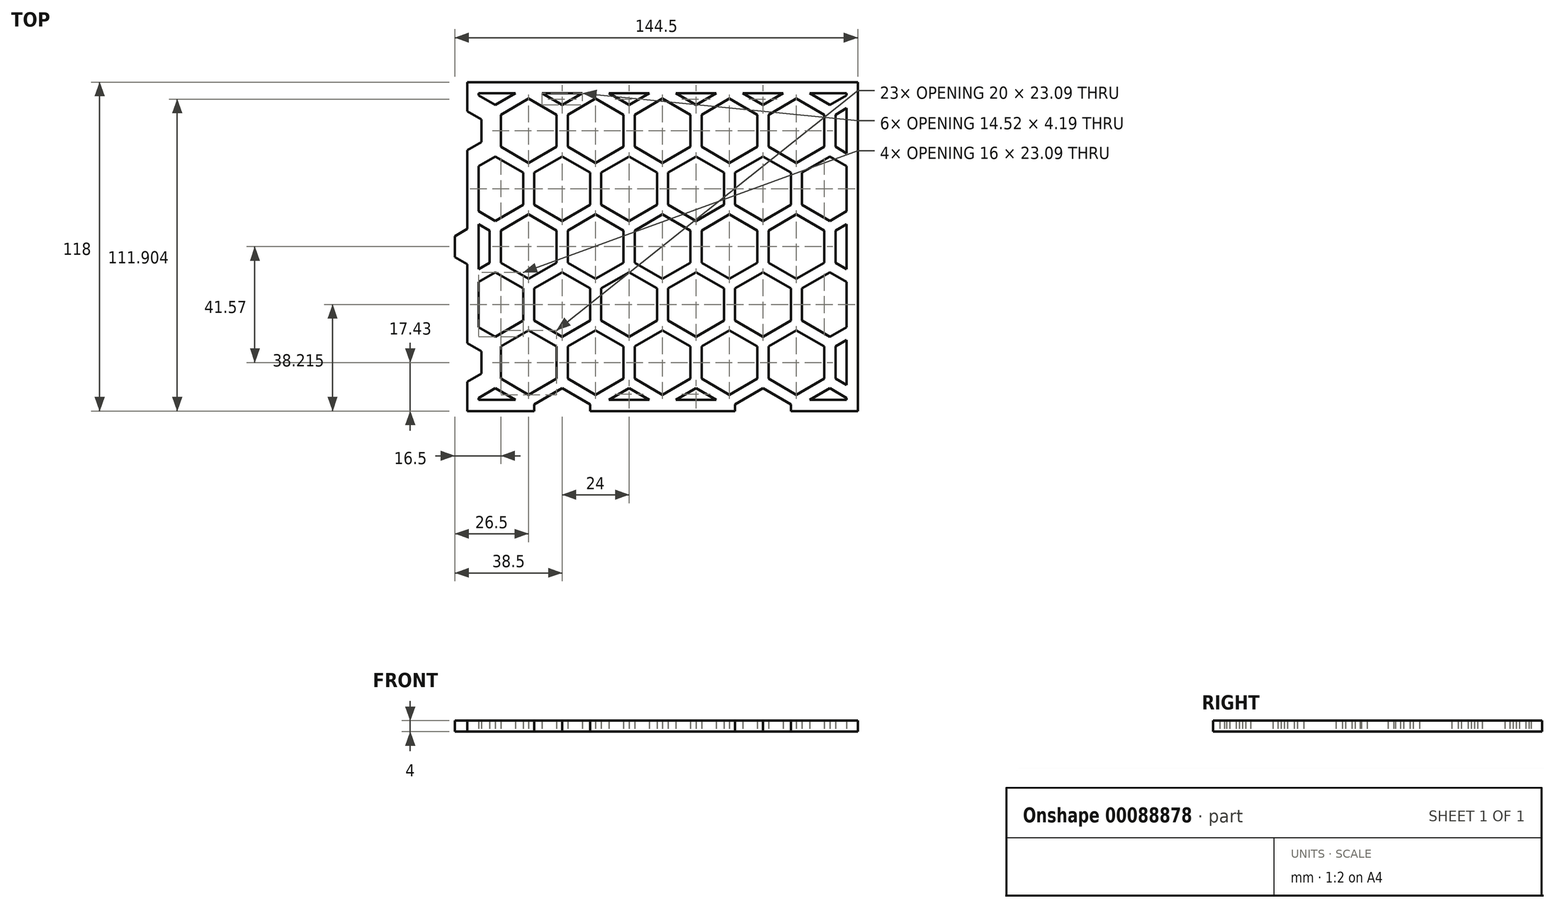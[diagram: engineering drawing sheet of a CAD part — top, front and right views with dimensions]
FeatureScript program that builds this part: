
annotation { "Feature Type Name" : "Feature", "Feature Type Description" : "" }
export const myFeature = defineFeature(function(context is Context, id is Id, definition is map)
    precondition{}
    {
        {
            var Q0;
            Q0=qCreatedBy(makeId("Top.planeOp"),FACE);
            var sketch = newSketch(context, id + "F0", { "sketchPlane" : qUnion([Q0])});
            skLineSegment(sketch, "E0.bottom", {"start": v(70, -59) * mm, "end": v(-70, -59) * mm});
            skLineSegment(sketch, "E0.top", {"start": v(70, 59) * mm, "end": v(-70, 59) * mm});
            skLineSegment(sketch, "E0.left", {"start": v(70, -59) * mm, "end": v(70, 59) * mm});
            skLineSegment(sketch, "E0.right", {"start": v(-70, -59) * mm, "end": v(-70, 59) * mm});
            skPoint(sketch, "E0.middle", {"position": v(0, 0) * mm});
            skLineSegment(sketch, "E1.0", {"start": v(-66, -55) * mm, "end": v(-66, 55) * mm});
            skLineSegment(sketch, "E1.1", {"start": v(66, -55) * mm, "end": v(-66, -55) * mm});
            skLineSegment(sketch, "E1.2", {"start": v(66, -55) * mm, "end": v(66, 55) * mm});
            skLineSegment(sketch, "E1.3", {"start": v(66, 55) * mm, "end": v(-66, 55) * mm});
            skSolve(sketch);
        }
        {
            var Q0;
            Q0 = qSketchRegion(id + "F0", true);
            extrude(context, id + "F1", {"entities" : qUnion([Q0]), "depth" : 4 * mm});
        }
        {
            var Q0;
            Q0=qCreatedBy(makeId("Top.planeOp"),FACE);
            var sketch = newSketch(context, id + "F2", { "sketchPlane" : qUnion([Q0])});
            skLineSegment(sketch, "E2.0.1.1", {"start": v(-62, -47.34) * mm, "end": v(-66, -49.65) * mm});
            skLineSegment(sketch, "E2.0.1.5", {"start": v(-66, -33.49) * mm, "end": v(-62, -35.8) * mm});
            skLineSegment(sketch, "E2.0.1.13", {"start": v(-62, -35.8) * mm, "end": v(-62, -47.34) * mm});
            skLineSegment(sketch, "E2.0.2.1", {"start": v(-62, -5.77) * mm, "end": v(-66, -8.08) * mm});
            skLineSegment(sketch, "E2.0.2.5", {"start": v(-66, 8.08) * mm, "end": v(-62, 5.77) * mm});
            skLineSegment(sketch, "E2.0.2.13", {"start": v(-62, 5.77) * mm, "end": v(-62, -5.77) * mm});
            skLineSegment(sketch, "E2.0.3.1", {"start": v(-62, 35.8) * mm, "end": v(-66, 33.49) * mm});
            skLineSegment(sketch, "E2.0.3.5", {"start": v(-66, 49.65) * mm, "end": v(-62, 47.34) * mm});
            skLineSegment(sketch, "E2.0.3.13", {"start": v(-62, 47.34) * mm, "end": v(-62, 35.8) * mm});
            skLineSegment(sketch, "E2.1.0.7", {"start": v(-60, -50.8) * mm, "end": v(-52.74, -55) * mm});
            skLineSegment(sketch, "E2.1.0.8", {"start": v(-66, -54.27) * mm, "end": v(-60, -50.8) * mm});
            skCircle(sketch, "E2.1.1.0", {"center": v(-48, -41.57) * mm, "radius": 11.55 * mm, "construction": true});
            skLineSegment(sketch, "E2.1.1.1", {"start": v(-38, -47.34) * mm, "end": v(-48, -53.12) * mm});
            skLineSegment(sketch, "E2.1.1.2", {"start": v(-48, -53.12) * mm, "end": v(-58, -47.34) * mm});
            skLineSegment(sketch, "E2.1.1.3", {"start": v(-58, -47.34) * mm, "end": v(-58, -35.8) * mm});
            skLineSegment(sketch, "E2.1.1.4", {"start": v(-58, -35.8) * mm, "end": v(-48, -30.02) * mm});
            skLineSegment(sketch, "E2.1.1.5", {"start": v(-48, -30.02) * mm, "end": v(-38, -35.8) * mm});
            skLineSegment(sketch, "E2.1.1.6", {"start": v(-50, -15.01) * mm, "end": v(-50, -26.56) * mm});
            skLineSegment(sketch, "E2.1.1.7", {"start": v(-60, -9.24) * mm, "end": v(-50, -15.01) * mm});
            skLineSegment(sketch, "E2.1.1.8", {"start": v(-66, -12.7) * mm, "end": v(-60, -9.24) * mm});
            skLineSegment(sketch, "E2.1.1.10", {"start": v(-60, -32.33) * mm, "end": v(-66, -28.87) * mm});
            skLineSegment(sketch, "E2.1.1.11", {"start": v(-50, -26.56) * mm, "end": v(-60, -32.33) * mm});
            skLineSegment(sketch, "E2.1.1.13", {"start": v(-38, -35.8) * mm, "end": v(-38, -47.34) * mm});
            skCircle(sketch, "E2.1.2.0", {"center": v(-48, 0) * mm, "radius": 11.55 * mm, "construction": true});
            skLineSegment(sketch, "E2.1.2.1", {"start": v(-38, -5.77) * mm, "end": v(-48, -11.55) * mm});
            skLineSegment(sketch, "E2.1.2.2", {"start": v(-48, -11.55) * mm, "end": v(-58, -5.77) * mm});
            skLineSegment(sketch, "E2.1.2.3", {"start": v(-58, -5.77) * mm, "end": v(-58, 5.77) * mm});
            skLineSegment(sketch, "E2.1.2.4", {"start": v(-58, 5.77) * mm, "end": v(-48, 11.55) * mm});
            skLineSegment(sketch, "E2.1.2.5", {"start": v(-48, 11.55) * mm, "end": v(-38, 5.77) * mm});
            skLineSegment(sketch, "E2.1.2.6", {"start": v(-50, 26.56) * mm, "end": v(-50, 15.01) * mm});
            skLineSegment(sketch, "E2.1.2.7", {"start": v(-60, 32.33) * mm, "end": v(-50, 26.56) * mm});
            skLineSegment(sketch, "E2.1.2.8", {"start": v(-66, 28.87) * mm, "end": v(-60, 32.33) * mm});
            skLineSegment(sketch, "E2.1.2.10", {"start": v(-60, 9.24) * mm, "end": v(-66, 12.7) * mm});
            skLineSegment(sketch, "E2.1.2.11", {"start": v(-50, 15.01) * mm, "end": v(-60, 9.24) * mm});
            skLineSegment(sketch, "E2.1.2.13", {"start": v(-38, 5.77) * mm, "end": v(-38, -5.77) * mm});
            skCircle(sketch, "E2.1.3.0", {"center": v(-48, 41.57) * mm, "radius": 11.55 * mm, "construction": true});
            skLineSegment(sketch, "E2.1.3.1", {"start": v(-38, 35.8) * mm, "end": v(-48, 30.02) * mm});
            skLineSegment(sketch, "E2.1.3.2", {"start": v(-48, 30.02) * mm, "end": v(-58, 35.8) * mm});
            skLineSegment(sketch, "E2.1.3.3", {"start": v(-58, 35.8) * mm, "end": v(-58, 47.34) * mm});
            skLineSegment(sketch, "E2.1.3.4", {"start": v(-58, 47.34) * mm, "end": v(-48, 53.12) * mm});
            skLineSegment(sketch, "E2.1.3.5", {"start": v(-48, 53.12) * mm, "end": v(-38, 47.34) * mm});
            skLineSegment(sketch, "E2.1.3.10", {"start": v(-60, 50.8) * mm, "end": v(-66, 54.27) * mm});
            skLineSegment(sketch, "E2.1.3.11", {"start": v(-52.74, 55) * mm, "end": v(-60, 50.8) * mm});
            skLineSegment(sketch, "E2.1.3.13", {"start": v(-38, 47.34) * mm, "end": v(-38, 35.8) * mm});
            skLineSegment(sketch, "E2.2.0.7", {"start": v(-36, -50.8) * mm, "end": v(-28.74, -55) * mm});
            skLineSegment(sketch, "E2.2.0.8", {"start": v(-43.26, -55) * mm, "end": v(-36, -50.8) * mm});
            skCircle(sketch, "E2.2.1.0", {"center": v(-24, -41.57) * mm, "radius": 11.55 * mm, "construction": true});
            skLineSegment(sketch, "E2.2.1.1", {"start": v(-14, -47.34) * mm, "end": v(-24, -53.12) * mm});
            skLineSegment(sketch, "E2.2.1.2", {"start": v(-24, -53.12) * mm, "end": v(-34, -47.34) * mm});
            skLineSegment(sketch, "E2.2.1.3", {"start": v(-34, -47.34) * mm, "end": v(-34, -35.8) * mm});
            skLineSegment(sketch, "E2.2.1.4", {"start": v(-34, -35.8) * mm, "end": v(-24, -30.02) * mm});
            skLineSegment(sketch, "E2.2.1.5", {"start": v(-24, -30.02) * mm, "end": v(-14, -35.8) * mm});
            skLineSegment(sketch, "E2.2.1.6", {"start": v(-26, -15.01) * mm, "end": v(-26, -26.56) * mm});
            skLineSegment(sketch, "E2.2.1.7", {"start": v(-36, -9.24) * mm, "end": v(-26, -15.01) * mm});
            skLineSegment(sketch, "E2.2.1.8", {"start": v(-46, -15.01) * mm, "end": v(-36, -9.24) * mm});
            skLineSegment(sketch, "E2.2.1.9", {"start": v(-46, -26.56) * mm, "end": v(-46, -15.01) * mm});
            skLineSegment(sketch, "E2.2.1.10", {"start": v(-36, -32.33) * mm, "end": v(-46, -26.56) * mm});
            skLineSegment(sketch, "E2.2.1.11", {"start": v(-26, -26.56) * mm, "end": v(-36, -32.33) * mm});
            skCircle(sketch, "E2.2.1.12", {"center": v(-36, -20.79) * mm, "radius": 11.55 * mm, "construction": true});
            skLineSegment(sketch, "E2.2.1.13", {"start": v(-14, -35.8) * mm, "end": v(-14, -47.34) * mm});
            skCircle(sketch, "E2.2.2.0", {"center": v(-24, 0) * mm, "radius": 11.55 * mm, "construction": true});
            skLineSegment(sketch, "E2.2.2.1", {"start": v(-14, -5.77) * mm, "end": v(-24, -11.55) * mm});
            skLineSegment(sketch, "E2.2.2.2", {"start": v(-24, -11.55) * mm, "end": v(-34, -5.77) * mm});
            skLineSegment(sketch, "E2.2.2.3", {"start": v(-34, -5.77) * mm, "end": v(-34, 5.77) * mm});
            skLineSegment(sketch, "E2.2.2.4", {"start": v(-34, 5.77) * mm, "end": v(-24, 11.55) * mm});
            skLineSegment(sketch, "E2.2.2.5", {"start": v(-24, 11.55) * mm, "end": v(-14, 5.77) * mm});
            skLineSegment(sketch, "E2.2.2.6", {"start": v(-26, 26.56) * mm, "end": v(-26, 15.01) * mm});
            skLineSegment(sketch, "E2.2.2.7", {"start": v(-36, 32.33) * mm, "end": v(-26, 26.56) * mm});
            skLineSegment(sketch, "E2.2.2.8", {"start": v(-46, 26.56) * mm, "end": v(-36, 32.33) * mm});
            skLineSegment(sketch, "E2.2.2.9", {"start": v(-46, 15.01) * mm, "end": v(-46, 26.56) * mm});
            skLineSegment(sketch, "E2.2.2.10", {"start": v(-36, 9.24) * mm, "end": v(-46, 15.01) * mm});
            skLineSegment(sketch, "E2.2.2.11", {"start": v(-26, 15.01) * mm, "end": v(-36, 9.24) * mm});
            skCircle(sketch, "E2.2.2.12", {"center": v(-36, 20.78) * mm, "radius": 11.55 * mm, "construction": true});
            skLineSegment(sketch, "E2.2.2.13", {"start": v(-14, 5.77) * mm, "end": v(-14, -5.77) * mm});
            skCircle(sketch, "E2.2.3.0", {"center": v(-24, 41.57) * mm, "radius": 11.55 * mm, "construction": true});
            skLineSegment(sketch, "E2.2.3.1", {"start": v(-14, 35.8) * mm, "end": v(-24, 30.02) * mm});
            skLineSegment(sketch, "E2.2.3.2", {"start": v(-24, 30.02) * mm, "end": v(-34, 35.8) * mm});
            skLineSegment(sketch, "E2.2.3.3", {"start": v(-34, 35.8) * mm, "end": v(-34, 47.34) * mm});
            skLineSegment(sketch, "E2.2.3.4", {"start": v(-34, 47.34) * mm, "end": v(-24, 53.12) * mm});
            skLineSegment(sketch, "E2.2.3.5", {"start": v(-24, 53.12) * mm, "end": v(-14, 47.34) * mm});
            skLineSegment(sketch, "E2.2.3.10", {"start": v(-36, 50.8) * mm, "end": v(-43.26, 55) * mm});
            skLineSegment(sketch, "E2.2.3.11", {"start": v(-28.74, 55) * mm, "end": v(-36, 50.8) * mm});
            skLineSegment(sketch, "E2.2.3.13", {"start": v(-14, 47.34) * mm, "end": v(-14, 35.8) * mm});
            skLineSegment(sketch, "E2.3.0.7", {"start": v(-12, -50.8) * mm, "end": v(-4.74, -55) * mm});
            skLineSegment(sketch, "E2.3.0.8", {"start": v(-19.26, -55) * mm, "end": v(-12, -50.8) * mm});
            skCircle(sketch, "E2.3.1.0", {"center": v(0, -41.57) * mm, "radius": 11.55 * mm, "construction": true});
            skLineSegment(sketch, "E2.3.1.1", {"start": v(10, -47.34) * mm, "end": v(0, -53.12) * mm});
            skLineSegment(sketch, "E2.3.1.2", {"start": v(0, -53.12) * mm, "end": v(-10, -47.34) * mm});
            skLineSegment(sketch, "E2.3.1.3", {"start": v(-10, -47.34) * mm, "end": v(-10, -35.8) * mm});
            skLineSegment(sketch, "E2.3.1.4", {"start": v(-10, -35.8) * mm, "end": v(0, -30.02) * mm});
            skLineSegment(sketch, "E2.3.1.5", {"start": v(0, -30.02) * mm, "end": v(10, -35.8) * mm});
            skLineSegment(sketch, "E2.3.1.6", {"start": v(-2, -15.01) * mm, "end": v(-2, -26.56) * mm});
            skLineSegment(sketch, "E2.3.1.7", {"start": v(-12, -9.24) * mm, "end": v(-2, -15.01) * mm});
            skLineSegment(sketch, "E2.3.1.8", {"start": v(-22, -15.01) * mm, "end": v(-12, -9.24) * mm});
            skLineSegment(sketch, "E2.3.1.9", {"start": v(-22, -26.56) * mm, "end": v(-22, -15.01) * mm});
            skLineSegment(sketch, "E2.3.1.10", {"start": v(-12, -32.33) * mm, "end": v(-22, -26.56) * mm});
            skLineSegment(sketch, "E2.3.1.11", {"start": v(-2, -26.56) * mm, "end": v(-12, -32.33) * mm});
            skCircle(sketch, "E2.3.1.12", {"center": v(-12, -20.79) * mm, "radius": 11.55 * mm, "construction": true});
            skLineSegment(sketch, "E2.3.1.13", {"start": v(10, -35.8) * mm, "end": v(10, -47.34) * mm});
            skCircle(sketch, "E2.3.2.0", {"center": v(0, 0) * mm, "radius": 11.55 * mm, "construction": true});
            skLineSegment(sketch, "E2.3.2.1", {"start": v(10, -5.77) * mm, "end": v(0, -11.55) * mm});
            skLineSegment(sketch, "E2.3.2.2", {"start": v(0, -11.55) * mm, "end": v(-10, -5.77) * mm});
            skLineSegment(sketch, "E2.3.2.3", {"start": v(-10, -5.77) * mm, "end": v(-10, 5.77) * mm});
            skLineSegment(sketch, "E2.3.2.4", {"start": v(-10, 5.77) * mm, "end": v(0, 11.55) * mm});
            skLineSegment(sketch, "E2.3.2.5", {"start": v(0, 11.55) * mm, "end": v(10, 5.77) * mm});
            skLineSegment(sketch, "E2.3.2.6", {"start": v(-2, 26.56) * mm, "end": v(-2, 15.01) * mm});
            skLineSegment(sketch, "E2.3.2.7", {"start": v(-12, 32.33) * mm, "end": v(-2, 26.56) * mm});
            skLineSegment(sketch, "E2.3.2.8", {"start": v(-22, 26.56) * mm, "end": v(-12, 32.33) * mm});
            skLineSegment(sketch, "E2.3.2.9", {"start": v(-22, 15.01) * mm, "end": v(-22, 26.56) * mm});
            skLineSegment(sketch, "E2.3.2.10", {"start": v(-12, 9.24) * mm, "end": v(-22, 15.01) * mm});
            skLineSegment(sketch, "E2.3.2.11", {"start": v(-2, 15.01) * mm, "end": v(-12, 9.24) * mm});
            skCircle(sketch, "E2.3.2.12", {"center": v(-12, 20.78) * mm, "radius": 11.55 * mm, "construction": true});
            skLineSegment(sketch, "E2.3.2.13", {"start": v(10, 5.77) * mm, "end": v(10, -5.77) * mm});
            skCircle(sketch, "E2.3.3.0", {"center": v(0, 41.57) * mm, "radius": 11.55 * mm, "construction": true});
            skLineSegment(sketch, "E2.3.3.1", {"start": v(10, 35.8) * mm, "end": v(0, 30.02) * mm});
            skLineSegment(sketch, "E2.3.3.2", {"start": v(0, 30.02) * mm, "end": v(-10, 35.8) * mm});
            skLineSegment(sketch, "E2.3.3.3", {"start": v(-10, 35.8) * mm, "end": v(-10, 47.34) * mm});
            skLineSegment(sketch, "E2.3.3.4", {"start": v(-10, 47.34) * mm, "end": v(0, 53.12) * mm});
            skLineSegment(sketch, "E2.3.3.5", {"start": v(0, 53.12) * mm, "end": v(10, 47.34) * mm});
            skLineSegment(sketch, "E2.3.3.10", {"start": v(-12, 50.8) * mm, "end": v(-19.26, 55) * mm});
            skLineSegment(sketch, "E2.3.3.11", {"start": v(-4.74, 55) * mm, "end": v(-12, 50.8) * mm});
            skLineSegment(sketch, "E2.3.3.13", {"start": v(10, 47.34) * mm, "end": v(10, 35.8) * mm});
            skLineSegment(sketch, "E2.4.0.7", {"start": v(12, -50.8) * mm, "end": v(19.26, -55) * mm});
            skLineSegment(sketch, "E2.4.0.8", {"start": v(4.74, -55) * mm, "end": v(12, -50.8) * mm});
            skCircle(sketch, "E2.4.1.0", {"center": v(24, -41.57) * mm, "radius": 11.55 * mm, "construction": true});
            skLineSegment(sketch, "E2.4.1.1", {"start": v(34, -47.34) * mm, "end": v(24, -53.12) * mm});
            skLineSegment(sketch, "E2.4.1.2", {"start": v(24, -53.12) * mm, "end": v(14, -47.34) * mm});
            skLineSegment(sketch, "E2.4.1.3", {"start": v(14, -47.34) * mm, "end": v(14, -35.8) * mm});
            skLineSegment(sketch, "E2.4.1.4", {"start": v(14, -35.8) * mm, "end": v(24, -30.02) * mm});
            skLineSegment(sketch, "E2.4.1.5", {"start": v(24, -30.02) * mm, "end": v(34, -35.8) * mm});
            skLineSegment(sketch, "E2.4.1.6", {"start": v(22, -15.01) * mm, "end": v(22, -26.56) * mm});
            skLineSegment(sketch, "E2.4.1.7", {"start": v(12, -9.24) * mm, "end": v(22, -15.01) * mm});
            skLineSegment(sketch, "E2.4.1.8", {"start": v(2, -15.01) * mm, "end": v(12, -9.24) * mm});
            skLineSegment(sketch, "E2.4.1.9", {"start": v(2, -26.56) * mm, "end": v(2, -15.01) * mm});
            skLineSegment(sketch, "E2.4.1.10", {"start": v(12, -32.33) * mm, "end": v(2, -26.56) * mm});
            skLineSegment(sketch, "E2.4.1.11", {"start": v(22, -26.56) * mm, "end": v(12, -32.33) * mm});
            skCircle(sketch, "E2.4.1.12", {"center": v(12, -20.79) * mm, "radius": 11.55 * mm, "construction": true});
            skLineSegment(sketch, "E2.4.1.13", {"start": v(34, -35.8) * mm, "end": v(34, -47.34) * mm});
            skCircle(sketch, "E2.4.2.0", {"center": v(24, 0) * mm, "radius": 11.55 * mm, "construction": true});
            skLineSegment(sketch, "E2.4.2.1", {"start": v(34, -5.77) * mm, "end": v(24, -11.55) * mm});
            skLineSegment(sketch, "E2.4.2.2", {"start": v(24, -11.55) * mm, "end": v(14, -5.77) * mm});
            skLineSegment(sketch, "E2.4.2.3", {"start": v(14, -5.77) * mm, "end": v(14, 5.77) * mm});
            skLineSegment(sketch, "E2.4.2.4", {"start": v(14, 5.77) * mm, "end": v(24, 11.55) * mm});
            skLineSegment(sketch, "E2.4.2.5", {"start": v(24, 11.55) * mm, "end": v(34, 5.77) * mm});
            skLineSegment(sketch, "E2.4.2.6", {"start": v(22, 26.56) * mm, "end": v(22, 15.01) * mm});
            skLineSegment(sketch, "E2.4.2.7", {"start": v(12, 32.33) * mm, "end": v(22, 26.56) * mm});
            skLineSegment(sketch, "E2.4.2.8", {"start": v(2, 26.56) * mm, "end": v(12, 32.33) * mm});
            skLineSegment(sketch, "E2.4.2.9", {"start": v(2, 15.01) * mm, "end": v(2, 26.56) * mm});
            skLineSegment(sketch, "E2.4.2.10", {"start": v(12, 9.24) * mm, "end": v(2, 15.01) * mm});
            skLineSegment(sketch, "E2.4.2.11", {"start": v(22, 15.01) * mm, "end": v(12, 9.24) * mm});
            skCircle(sketch, "E2.4.2.12", {"center": v(12, 20.78) * mm, "radius": 11.55 * mm, "construction": true});
            skLineSegment(sketch, "E2.4.2.13", {"start": v(34, 5.77) * mm, "end": v(34, -5.77) * mm});
            skCircle(sketch, "E2.4.3.0", {"center": v(24, 41.57) * mm, "radius": 11.55 * mm, "construction": true});
            skLineSegment(sketch, "E2.4.3.1", {"start": v(34, 35.8) * mm, "end": v(24, 30.02) * mm});
            skLineSegment(sketch, "E2.4.3.2", {"start": v(24, 30.02) * mm, "end": v(14, 35.8) * mm});
            skLineSegment(sketch, "E2.4.3.3", {"start": v(14, 35.8) * mm, "end": v(14, 47.34) * mm});
            skLineSegment(sketch, "E2.4.3.4", {"start": v(14, 47.34) * mm, "end": v(24, 53.12) * mm});
            skLineSegment(sketch, "E2.4.3.5", {"start": v(24, 53.12) * mm, "end": v(34, 47.34) * mm});
            skLineSegment(sketch, "E2.4.3.10", {"start": v(12, 50.8) * mm, "end": v(4.74, 55) * mm});
            skLineSegment(sketch, "E2.4.3.11", {"start": v(19.26, 55) * mm, "end": v(12, 50.8) * mm});
            skLineSegment(sketch, "E2.4.3.13", {"start": v(34, 47.34) * mm, "end": v(34, 35.8) * mm});
            skLineSegment(sketch, "E2.5.0.7", {"start": v(36, -50.8) * mm, "end": v(43.26, -55) * mm});
            skLineSegment(sketch, "E2.5.0.8", {"start": v(28.74, -55) * mm, "end": v(36, -50.8) * mm});
            skCircle(sketch, "E2.5.1.0", {"center": v(48, -41.57) * mm, "radius": 11.55 * mm, "construction": true});
            skLineSegment(sketch, "E2.5.1.1", {"start": v(58, -47.34) * mm, "end": v(48, -53.12) * mm});
            skLineSegment(sketch, "E2.5.1.2", {"start": v(48, -53.12) * mm, "end": v(38, -47.34) * mm});
            skLineSegment(sketch, "E2.5.1.3", {"start": v(38, -47.34) * mm, "end": v(38, -35.8) * mm});
            skLineSegment(sketch, "E2.5.1.4", {"start": v(38, -35.8) * mm, "end": v(48, -30.02) * mm});
            skLineSegment(sketch, "E2.5.1.5", {"start": v(48, -30.02) * mm, "end": v(58, -35.8) * mm});
            skLineSegment(sketch, "E2.5.1.6", {"start": v(46, -15.01) * mm, "end": v(46, -26.56) * mm});
            skLineSegment(sketch, "E2.5.1.7", {"start": v(36, -9.24) * mm, "end": v(46, -15.01) * mm});
            skLineSegment(sketch, "E2.5.1.8", {"start": v(26, -15.01) * mm, "end": v(36, -9.24) * mm});
            skLineSegment(sketch, "E2.5.1.9", {"start": v(26, -26.56) * mm, "end": v(26, -15.01) * mm});
            skLineSegment(sketch, "E2.5.1.10", {"start": v(36, -32.33) * mm, "end": v(26, -26.56) * mm});
            skLineSegment(sketch, "E2.5.1.11", {"start": v(46, -26.56) * mm, "end": v(36, -32.33) * mm});
            skCircle(sketch, "E2.5.1.12", {"center": v(36, -20.79) * mm, "radius": 11.55 * mm, "construction": true});
            skLineSegment(sketch, "E2.5.1.13", {"start": v(58, -35.8) * mm, "end": v(58, -47.34) * mm});
            skCircle(sketch, "E2.5.2.0", {"center": v(48, 0) * mm, "radius": 11.55 * mm, "construction": true});
            skLineSegment(sketch, "E2.5.2.1", {"start": v(58, -5.77) * mm, "end": v(48, -11.55) * mm});
            skLineSegment(sketch, "E2.5.2.2", {"start": v(48, -11.55) * mm, "end": v(38, -5.77) * mm});
            skLineSegment(sketch, "E2.5.2.3", {"start": v(38, -5.77) * mm, "end": v(38, 5.77) * mm});
            skLineSegment(sketch, "E2.5.2.4", {"start": v(38, 5.77) * mm, "end": v(48, 11.55) * mm});
            skLineSegment(sketch, "E2.5.2.5", {"start": v(48, 11.55) * mm, "end": v(58, 5.77) * mm});
            skLineSegment(sketch, "E2.5.2.6", {"start": v(46, 26.56) * mm, "end": v(46, 15.01) * mm});
            skLineSegment(sketch, "E2.5.2.7", {"start": v(36, 32.33) * mm, "end": v(46, 26.56) * mm});
            skLineSegment(sketch, "E2.5.2.8", {"start": v(26, 26.56) * mm, "end": v(36, 32.33) * mm});
            skLineSegment(sketch, "E2.5.2.9", {"start": v(26, 15.01) * mm, "end": v(26, 26.56) * mm});
            skLineSegment(sketch, "E2.5.2.10", {"start": v(36, 9.24) * mm, "end": v(26, 15.01) * mm});
            skLineSegment(sketch, "E2.5.2.11", {"start": v(46, 15.01) * mm, "end": v(36, 9.24) * mm});
            skCircle(sketch, "E2.5.2.12", {"center": v(36, 20.78) * mm, "radius": 11.55 * mm, "construction": true});
            skLineSegment(sketch, "E2.5.2.13", {"start": v(58, 5.77) * mm, "end": v(58, -5.77) * mm});
            skCircle(sketch, "E2.5.3.0", {"center": v(48, 41.57) * mm, "radius": 11.55 * mm, "construction": true});
            skLineSegment(sketch, "E2.5.3.1", {"start": v(58, 35.8) * mm, "end": v(48, 30.02) * mm});
            skLineSegment(sketch, "E2.5.3.2", {"start": v(48, 30.02) * mm, "end": v(38, 35.8) * mm});
            skLineSegment(sketch, "E2.5.3.3", {"start": v(38, 35.8) * mm, "end": v(38, 47.34) * mm});
            skLineSegment(sketch, "E2.5.3.4", {"start": v(38, 47.34) * mm, "end": v(48, 53.12) * mm});
            skLineSegment(sketch, "E2.5.3.5", {"start": v(48, 53.12) * mm, "end": v(58, 47.34) * mm});
            skLineSegment(sketch, "E2.5.3.10", {"start": v(36, 50.8) * mm, "end": v(28.74, 55) * mm});
            skLineSegment(sketch, "E2.5.3.11", {"start": v(43.26, 55) * mm, "end": v(36, 50.8) * mm});
            skLineSegment(sketch, "E2.5.3.13", {"start": v(58, 47.34) * mm, "end": v(58, 35.8) * mm});
            skLineSegment(sketch, "E2.6.0.7", {"start": v(60, -50.8) * mm, "end": v(66, -54.27) * mm});
            skLineSegment(sketch, "E2.6.0.8", {"start": v(52.74, -55) * mm, "end": v(60, -50.8) * mm});
            skLineSegment(sketch, "E2.6.1.2", {"start": v(66, -49.65) * mm, "end": v(62, -47.34) * mm});
            skLineSegment(sketch, "E2.6.1.3", {"start": v(62, -47.34) * mm, "end": v(62, -35.8) * mm});
            skLineSegment(sketch, "E2.6.1.4", {"start": v(62, -35.8) * mm, "end": v(66, -33.49) * mm});
            skLineSegment(sketch, "E2.6.1.7", {"start": v(60, -9.24) * mm, "end": v(66, -12.7) * mm});
            skLineSegment(sketch, "E2.6.1.8", {"start": v(50, -15.01) * mm, "end": v(60, -9.24) * mm});
            skLineSegment(sketch, "E2.6.1.9", {"start": v(50, -26.56) * mm, "end": v(50, -15.01) * mm});
            skLineSegment(sketch, "E2.6.1.10", {"start": v(60, -32.33) * mm, "end": v(50, -26.56) * mm});
            skLineSegment(sketch, "E2.6.1.11", {"start": v(66, -28.87) * mm, "end": v(60, -32.33) * mm});
            skLineSegment(sketch, "E2.6.2.2", {"start": v(66, -8.08) * mm, "end": v(62, -5.77) * mm});
            skLineSegment(sketch, "E2.6.2.3", {"start": v(62, -5.77) * mm, "end": v(62, 5.77) * mm});
            skLineSegment(sketch, "E2.6.2.4", {"start": v(62, 5.77) * mm, "end": v(66, 8.08) * mm});
            skLineSegment(sketch, "E2.6.2.7", {"start": v(60, 32.33) * mm, "end": v(66, 28.87) * mm});
            skLineSegment(sketch, "E2.6.2.8", {"start": v(50, 26.56) * mm, "end": v(60, 32.33) * mm});
            skLineSegment(sketch, "E2.6.2.9", {"start": v(50, 15.01) * mm, "end": v(50, 26.56) * mm});
            skLineSegment(sketch, "E2.6.2.10", {"start": v(60, 9.24) * mm, "end": v(50, 15.01) * mm});
            skLineSegment(sketch, "E2.6.2.11", {"start": v(66, 12.7) * mm, "end": v(60, 9.24) * mm});
            skLineSegment(sketch, "E2.6.3.2", {"start": v(66, 33.49) * mm, "end": v(62, 35.8) * mm});
            skLineSegment(sketch, "E2.6.3.3", {"start": v(62, 35.8) * mm, "end": v(62, 47.34) * mm});
            skLineSegment(sketch, "E2.6.3.4", {"start": v(62, 47.34) * mm, "end": v(66, 49.65) * mm});
            skLineSegment(sketch, "E2.6.3.10", {"start": v(60, 50.8) * mm, "end": v(52.74, 55) * mm});
            skLineSegment(sketch, "E2.6.3.11", {"start": v(66, 54.27) * mm, "end": v(60, 50.8) * mm});
            skLineSegment(sketch, "E3.0", {"start": v(-66, -55) * mm, "end": v(-66, -54.27) * mm});
            skLineSegment(sketch, "E3.1", {"start": v(66, 55) * mm, "end": v(52.74, 55) * mm});
            skLineSegment(sketch, "E3.2", {"start": v(66, -55) * mm, "end": v(66, -54.27) * mm});
            skLineSegment(sketch, "E3.3", {"start": v(66, -55) * mm, "end": v(52.74, -55) * mm});
            skLineSegment(sketch, "E4.trimOffspring", {"start": v(-66, 54.27) * mm, "end": v(-66, 55) * mm});
            skLineSegment(sketch, "E5.trimOffspring", {"start": v(-66, 33.49) * mm, "end": v(-66, 49.65) * mm});
            skLineSegment(sketch, "E6.trimOffspring", {"start": v(-66, 12.7) * mm, "end": v(-66, 28.87) * mm});
            skLineSegment(sketch, "E7.trimOffspring", {"start": v(-52.74, 55) * mm, "end": v(-66, 55) * mm});
            skLineSegment(sketch, "E8.trimOffspring", {"start": v(-28.74, 55) * mm, "end": v(-43.26, 55) * mm});
            skLineSegment(sketch, "E9.trimOffspring", {"start": v(-4.74, 55) * mm, "end": v(-19.26, 55) * mm});
            skLineSegment(sketch, "E10.trimOffspring", {"start": v(19.26, 55) * mm, "end": v(4.74, 55) * mm});
            skLineSegment(sketch, "E11.trimOffspring", {"start": v(43.26, 55) * mm, "end": v(28.74, 55) * mm});
            skLineSegment(sketch, "E12.trimOffspring", {"start": v(66, 54.27) * mm, "end": v(66, 55) * mm});
            skLineSegment(sketch, "E13.trimOffspring", {"start": v(66, 33.49) * mm, "end": v(66, 49.65) * mm});
            skLineSegment(sketch, "E14.trimOffspring", {"start": v(66, 12.7) * mm, "end": v(66, 28.87) * mm});
            skLineSegment(sketch, "E15.trimOffspring", {"start": v(66, -8.08) * mm, "end": v(66, 8.08) * mm});
            skLineSegment(sketch, "E16.trimOffspring", {"start": v(66, -28.87) * mm, "end": v(66, -12.7) * mm});
            skLineSegment(sketch, "E17.trimOffspring", {"start": v(66, -49.65) * mm, "end": v(66, -33.49) * mm});
            skLineSegment(sketch, "E18.trimOffspring", {"start": v(43.26, -55) * mm, "end": v(28.74, -55) * mm});
            skLineSegment(sketch, "E19.trimOffspring", {"start": v(19.26, -55) * mm, "end": v(4.74, -55) * mm});
            skLineSegment(sketch, "E20.trimOffspring", {"start": v(-4.74, -55) * mm, "end": v(-19.26, -55) * mm});
            skLineSegment(sketch, "E21.trimOffspring", {"start": v(-28.74, -55) * mm, "end": v(-43.26, -55) * mm});
            skLineSegment(sketch, "E22.trimOffspring", {"start": v(-52.74, -55) * mm, "end": v(-66, -55) * mm});
            skLineSegment(sketch, "E23.trimOffspring", {"start": v(-66, -49.65) * mm, "end": v(-66, -33.49) * mm});
            skLineSegment(sketch, "E24.trimOffspring", {"start": v(-66, -28.87) * mm, "end": v(-66, -12.7) * mm});
            skLineSegment(sketch, "E25.trimOffspring", {"start": v(-66, -8.08) * mm, "end": v(-66, 8.08) * mm});
            skLineSegment(sketch, "E26.0", {"start": v(-70, -59) * mm, "end": v(-70, 59) * mm});
            skLineSegment(sketch, "E26.1", {"start": v(70, 59) * mm, "end": v(-70, 59) * mm});
            skLineSegment(sketch, "E26.2", {"start": v(70, -59) * mm, "end": v(70, 59) * mm});
            skLineSegment(sketch, "E26.3", {"start": v(70, -59) * mm, "end": v(-70, -59) * mm});
            skSolve(sketch);
        }
        {
            var Q0;
            Q0 = qSketchRegion(id + "F2", true);
            var Q1;
            Q1=makeQuery(id+"F1.opExtrude","CAP_FACE",FACE,{"disambiguationData":[OSD([sQuery(id+"F0.wireOp",EDGE,"E0.bottom"),sQuery(id+"F0.wireOp",EDGE,"E0.top"),sQuery(id+"F0.wireOp",EDGE,"E0.left"),sQuery(id+"F0.wireOp",EDGE,"E0.right"),sQuery(id+"F0.wireOp",EDGE,"E1.0"),sQuery(id+"F0.wireOp",EDGE,"E1.1"),sQuery(id+"F0.wireOp",EDGE,"E1.2"),sQuery(id+"F0.wireOp",EDGE,"E1.3")])],"isStart":false});
            extrude(context, id + "F3", {"entities" : qUnion([Q0]), "operationType" : NewBodyOperationType.ADD, "endBound" : BoundingType.UP_TO_SURFACE, "endBoundEntityFace" : qUnion([Q1]), "depth" : 4 * mm});
        }
        {
            var Q0;
            Q0=qCreatedBy(makeId("Top.planeOp"),FACE);
            var sketch = newSketch(context, id + "F4", { "sketchPlane" : qUnion([Q0])});
            skCircle(sketch, "E27.cCircle", {"center": v(36, -62.36) * mm, "radius": 11.55 * mm, "construction": true});
            skLineSegment(sketch, "E27.0", {"start": v(36, -73.9) * mm, "end": v(26, -68.13) * mm});
            skLineSegment(sketch, "E27.1", {"start": v(26, -68.13) * mm, "end": v(26, -56.58) * mm});
            skLineSegment(sketch, "E27.2", {"start": v(26, -56.58) * mm, "end": v(36, -50.8) * mm});
            skLineSegment(sketch, "E27.3", {"start": v(36, -50.8) * mm, "end": v(46, -56.58) * mm});
            skLineSegment(sketch, "E27.4", {"start": v(46, -56.58) * mm, "end": v(46, -68.13) * mm});
            skLineSegment(sketch, "E27.5", {"start": v(46, -68.13) * mm, "end": v(36, -73.9) * mm});
            skCircle(sketch, "E28.cCircle", {"center": v(-36, -62.36) * mm, "radius": 11.55 * mm, "construction": true});
            skLineSegment(sketch, "E28.0", {"start": v(-26, -68.13) * mm, "end": v(-36, -73.9) * mm});
            skLineSegment(sketch, "E28.1", {"start": v(-36, -73.9) * mm, "end": v(-46, -68.13) * mm});
            skLineSegment(sketch, "E28.2", {"start": v(-46, -68.13) * mm, "end": v(-46, -56.58) * mm});
            skLineSegment(sketch, "E28.3", {"start": v(-46, -56.58) * mm, "end": v(-36, -50.8) * mm});
            skLineSegment(sketch, "E28.4", {"start": v(-36, -50.8) * mm, "end": v(-26, -56.58) * mm});
            skLineSegment(sketch, "E28.5", {"start": v(-26, -56.58) * mm, "end": v(-26, -68.13) * mm});
            skSolve(sketch);
        }
        {
            var Q0;
            Q0 = qSketchRegion(id + "F4", true);
            extrude(context, id + "F5", {"entities" : qUnion([Q0]), "operationType" : NewBodyOperationType.REMOVE, "endBound" : BoundingType.THROUGH_ALL, "depth" : 25 * mm});
        }
        {
            var Q0;
            Q0=qCreatedBy(makeId("Top.planeOp"),FACE);
            var sketch = newSketch(context, id + "F6", { "sketchPlane" : qUnion([Q0])});
            skCircle(sketch, "E29.cCircle", {"center": v(-68, 0) * mm, "radius": 11.55 * mm, "construction": true});
            skLineSegment(sketch, "E29.1", {"start": v(-70, -10.4) * mm, "end": v(-78, -5.77) * mm, "construction": true});
            skLineSegment(sketch, "E29.2", {"start": v(-78, -5.77) * mm, "end": v(-78, 5.77) * mm, "construction": true});
            skLineSegment(sketch, "E29.3", {"start": v(-78, 5.77) * mm, "end": v(-70, 10.4) * mm, "construction": true});
            skLineSegment(sketch, "E29.5", {"start": v(-58, 5.77) * mm, "end": v(-58, -5.77) * mm});
            skLineSegment(sketch, "E30.0", {"start": v(-70, -59) * mm, "end": v(-70, -59) * mm});
            skPoint(sketch, "E31.orphan", {"position": v(-68, -11.55) * mm});
            skLineSegment(sketch, "E32.0", {"start": v(-74.5, 3.75) * mm, "end": v(-68.25, 7.36) * mm});
            skLineSegment(sketch, "E32.1", {"start": v(-74.5, -3.75) * mm, "end": v(-74.5, 3.75) * mm});
            skLineSegment(sketch, "E32.2", {"start": v(-68.25, -7.36) * mm, "end": v(-74.5, -3.75) * mm});
            skLineSegment(sketch, "E33.0", {"start": v(-70, -59) * mm, "end": v(-70, 59) * mm});
            skSolve(sketch);
        }
        {
            var Q0;
            Q0 = qSketchRegion(id + "F6", true);
            var Q1;
            Q1=makeQuery(id+"F3.boolean.opBoolean","MERGE",FACE,{"derivedFrom":[makeQuery(id+"F1.opExtrude","CAP_FACE",FACE,{"disambiguationData":[OSD([sQuery(id+"F0.wireOp",EDGE,"E0.bottom"),sQuery(id+"F0.wireOp",EDGE,"E0.top"),sQuery(id+"F0.wireOp",EDGE,"E0.left"),sQuery(id+"F0.wireOp",EDGE,"E0.right"),sQuery(id+"F0.wireOp",EDGE,"E1.0"),sQuery(id+"F0.wireOp",EDGE,"E1.1"),sQuery(id+"F0.wireOp",EDGE,"E1.2"),sQuery(id+"F0.wireOp",EDGE,"E1.3")])],"isStart":false}),makeQuery(id+"F3.opExtrude","CAP_FACE",FACE,{"disambiguationData":[OSD([sQuery(id+"F2.wireOp",EDGE,"E2.0.1.1"),sQuery(id+"F2.wireOp",EDGE,"E2.0.1.5"),sQuery(id+"F2.wireOp",EDGE,"E2.0.1.13"),sQuery(id+"F2.wireOp",EDGE,"E2.0.2.1"),sQuery(id+"F2.wireOp",EDGE,"E2.0.2.5"),sQuery(id+"F2.wireOp",EDGE,"E2.0.2.13"),sQuery(id+"F2.wireOp",EDGE,"E2.0.3.1"),sQuery(id+"F2.wireOp",EDGE,"E2.0.3.5"),sQuery(id+"F2.wireOp",EDGE,"E2.0.3.13"),sQuery(id+"F2.wireOp",EDGE,"E2.1.0.7"),sQuery(id+"F2.wireOp",EDGE,"E2.1.0.8"),sQuery(id+"F2.wireOp",EDGE,"E2.1.1.1"),sQuery(id+"F2.wireOp",EDGE,"E2.1.1.2"),sQuery(id+"F2.wireOp",EDGE,"E2.1.1.3"),sQuery(id+"F2.wireOp",EDGE,"E2.1.1.4"),sQuery(id+"F2.wireOp",EDGE,"E2.1.1.5"),sQuery(id+"F2.wireOp",EDGE,"E2.1.1.6"),sQuery(id+"F2.wireOp",EDGE,"E2.1.1.7"),sQuery(id+"F2.wireOp",EDGE,"E2.1.1.8"),sQuery(id+"F2.wireOp",EDGE,"E2.1.1.10"),sQuery(id+"F2.wireOp",EDGE,"E2.1.1.11"),sQuery(id+"F2.wireOp",EDGE,"E2.1.1.13"),sQuery(id+"F2.wireOp",EDGE,"E2.1.2.1"),sQuery(id+"F2.wireOp",EDGE,"E2.1.2.2"),sQuery(id+"F2.wireOp",EDGE,"E2.1.2.3"),sQuery(id+"F2.wireOp",EDGE,"E2.1.2.4"),sQuery(id+"F2.wireOp",EDGE,"E2.1.2.5"),sQuery(id+"F2.wireOp",EDGE,"E2.1.2.6"),sQuery(id+"F2.wireOp",EDGE,"E2.1.2.7"),sQuery(id+"F2.wireOp",EDGE,"E2.1.2.8"),sQuery(id+"F2.wireOp",EDGE,"E2.1.2.10"),sQuery(id+"F2.wireOp",EDGE,"E2.1.2.11"),sQuery(id+"F2.wireOp",EDGE,"E2.1.2.13"),sQuery(id+"F2.wireOp",EDGE,"E2.1.3.1"),sQuery(id+"F2.wireOp",EDGE,"E2.1.3.2"),sQuery(id+"F2.wireOp",EDGE,"E2.1.3.3"),sQuery(id+"F2.wireOp",EDGE,"E2.1.3.4"),sQuery(id+"F2.wireOp",EDGE,"E2.1.3.5"),sQuery(id+"F2.wireOp",EDGE,"E2.1.3.10"),sQuery(id+"F2.wireOp",EDGE,"E2.1.3.11"),sQuery(id+"F2.wireOp",EDGE,"E2.1.3.13"),sQuery(id+"F2.wireOp",EDGE,"E2.2.0.7"),sQuery(id+"F2.wireOp",EDGE,"E2.2.0.8"),sQuery(id+"F2.wireOp",EDGE,"E2.2.1.1"),sQuery(id+"F2.wireOp",EDGE,"E2.2.1.2"),sQuery(id+"F2.wireOp",EDGE,"E2.2.1.3"),sQuery(id+"F2.wireOp",EDGE,"E2.2.1.4"),sQuery(id+"F2.wireOp",EDGE,"E2.2.1.5"),sQuery(id+"F2.wireOp",EDGE,"E2.2.1.6"),sQuery(id+"F2.wireOp",EDGE,"E2.2.1.7"),sQuery(id+"F2.wireOp",EDGE,"E2.2.1.8"),sQuery(id+"F2.wireOp",EDGE,"E2.2.1.9"),sQuery(id+"F2.wireOp",EDGE,"E2.2.1.10"),sQuery(id+"F2.wireOp",EDGE,"E2.2.1.11"),sQuery(id+"F2.wireOp",EDGE,"E2.2.1.13"),sQuery(id+"F2.wireOp",EDGE,"E2.2.2.1"),sQuery(id+"F2.wireOp",EDGE,"E2.2.2.2"),sQuery(id+"F2.wireOp",EDGE,"E2.2.2.3"),sQuery(id+"F2.wireOp",EDGE,"E2.2.2.4"),sQuery(id+"F2.wireOp",EDGE,"E2.2.2.5"),sQuery(id+"F2.wireOp",EDGE,"E2.2.2.6"),sQuery(id+"F2.wireOp",EDGE,"E2.2.2.7"),sQuery(id+"F2.wireOp",EDGE,"E2.2.2.8"),sQuery(id+"F2.wireOp",EDGE,"E2.2.2.9"),sQuery(id+"F2.wireOp",EDGE,"E2.2.2.10"),sQuery(id+"F2.wireOp",EDGE,"E2.2.2.11"),sQuery(id+"F2.wireOp",EDGE,"E2.2.2.13"),sQuery(id+"F2.wireOp",EDGE,"E2.2.3.1"),sQuery(id+"F2.wireOp",EDGE,"E2.2.3.2"),sQuery(id+"F2.wireOp",EDGE,"E2.2.3.3"),sQuery(id+"F2.wireOp",EDGE,"E2.2.3.4"),sQuery(id+"F2.wireOp",EDGE,"E2.2.3.5"),sQuery(id+"F2.wireOp",EDGE,"E2.2.3.10"),sQuery(id+"F2.wireOp",EDGE,"E2.2.3.11"),sQuery(id+"F2.wireOp",EDGE,"E2.2.3.13"),sQuery(id+"F2.wireOp",EDGE,"E2.3.0.7"),sQuery(id+"F2.wireOp",EDGE,"E2.3.0.8"),sQuery(id+"F2.wireOp",EDGE,"E2.3.1.1"),sQuery(id+"F2.wireOp",EDGE,"E2.3.1.2"),sQuery(id+"F2.wireOp",EDGE,"E2.3.1.3"),sQuery(id+"F2.wireOp",EDGE,"E2.3.1.4"),sQuery(id+"F2.wireOp",EDGE,"E2.3.1.5"),sQuery(id+"F2.wireOp",EDGE,"E2.3.1.6"),sQuery(id+"F2.wireOp",EDGE,"E2.3.1.7"),sQuery(id+"F2.wireOp",EDGE,"E2.3.1.8"),sQuery(id+"F2.wireOp",EDGE,"E2.3.1.9"),sQuery(id+"F2.wireOp",EDGE,"E2.3.1.10"),sQuery(id+"F2.wireOp",EDGE,"E2.3.1.11"),sQuery(id+"F2.wireOp",EDGE,"E2.3.1.13"),sQuery(id+"F2.wireOp",EDGE,"E2.3.2.1"),sQuery(id+"F2.wireOp",EDGE,"E2.3.2.2"),sQuery(id+"F2.wireOp",EDGE,"E2.3.2.3"),sQuery(id+"F2.wireOp",EDGE,"E2.3.2.4"),sQuery(id+"F2.wireOp",EDGE,"E2.3.2.5"),sQuery(id+"F2.wireOp",EDGE,"E2.3.2.6"),sQuery(id+"F2.wireOp",EDGE,"E2.3.2.7"),sQuery(id+"F2.wireOp",EDGE,"E2.3.2.8"),sQuery(id+"F2.wireOp",EDGE,"E2.3.2.9"),sQuery(id+"F2.wireOp",EDGE,"E2.3.2.10"),sQuery(id+"F2.wireOp",EDGE,"E2.3.2.11"),sQuery(id+"F2.wireOp",EDGE,"E2.3.2.13"),sQuery(id+"F2.wireOp",EDGE,"E2.3.3.1"),sQuery(id+"F2.wireOp",EDGE,"E2.3.3.2"),sQuery(id+"F2.wireOp",EDGE,"E2.3.3.3"),sQuery(id+"F2.wireOp",EDGE,"E2.3.3.4"),sQuery(id+"F2.wireOp",EDGE,"E2.3.3.5"),sQuery(id+"F2.wireOp",EDGE,"E2.3.3.10"),sQuery(id+"F2.wireOp",EDGE,"E2.3.3.11"),sQuery(id+"F2.wireOp",EDGE,"E2.3.3.13"),sQuery(id+"F2.wireOp",EDGE,"E2.4.0.7"),sQuery(id+"F2.wireOp",EDGE,"E2.4.0.8"),sQuery(id+"F2.wireOp",EDGE,"E2.4.1.1"),sQuery(id+"F2.wireOp",EDGE,"E2.4.1.2"),sQuery(id+"F2.wireOp",EDGE,"E2.4.1.3"),sQuery(id+"F2.wireOp",EDGE,"E2.4.1.4"),sQuery(id+"F2.wireOp",EDGE,"E2.4.1.5"),sQuery(id+"F2.wireOp",EDGE,"E2.4.1.6"),sQuery(id+"F2.wireOp",EDGE,"E2.4.1.7"),sQuery(id+"F2.wireOp",EDGE,"E2.4.1.8"),sQuery(id+"F2.wireOp",EDGE,"E2.4.1.9"),sQuery(id+"F2.wireOp",EDGE,"E2.4.1.10"),sQuery(id+"F2.wireOp",EDGE,"E2.4.1.11"),sQuery(id+"F2.wireOp",EDGE,"E2.4.1.13"),sQuery(id+"F2.wireOp",EDGE,"E2.4.2.1"),sQuery(id+"F2.wireOp",EDGE,"E2.4.2.2"),sQuery(id+"F2.wireOp",EDGE,"E2.4.2.3"),sQuery(id+"F2.wireOp",EDGE,"E2.4.2.4"),sQuery(id+"F2.wireOp",EDGE,"E2.4.2.5"),sQuery(id+"F2.wireOp",EDGE,"E2.4.2.6"),sQuery(id+"F2.wireOp",EDGE,"E2.4.2.7"),sQuery(id+"F2.wireOp",EDGE,"E2.4.2.8"),sQuery(id+"F2.wireOp",EDGE,"E2.4.2.9"),sQuery(id+"F2.wireOp",EDGE,"E2.4.2.10"),sQuery(id+"F2.wireOp",EDGE,"E2.4.2.11"),sQuery(id+"F2.wireOp",EDGE,"E2.4.2.13"),sQuery(id+"F2.wireOp",EDGE,"E2.4.3.1"),sQuery(id+"F2.wireOp",EDGE,"E2.4.3.2"),sQuery(id+"F2.wireOp",EDGE,"E2.4.3.3"),sQuery(id+"F2.wireOp",EDGE,"E2.4.3.4"),sQuery(id+"F2.wireOp",EDGE,"E2.4.3.5"),sQuery(id+"F2.wireOp",EDGE,"E2.4.3.10"),sQuery(id+"F2.wireOp",EDGE,"E2.4.3.11"),sQuery(id+"F2.wireOp",EDGE,"E2.4.3.13"),sQuery(id+"F2.wireOp",EDGE,"E2.5.0.7"),sQuery(id+"F2.wireOp",EDGE,"E2.5.0.8"),sQuery(id+"F2.wireOp",EDGE,"E2.5.1.1"),sQuery(id+"F2.wireOp",EDGE,"E2.5.1.2"),sQuery(id+"F2.wireOp",EDGE,"E2.5.1.3"),sQuery(id+"F2.wireOp",EDGE,"E2.5.1.4"),sQuery(id+"F2.wireOp",EDGE,"E2.5.1.5"),sQuery(id+"F2.wireOp",EDGE,"E2.5.1.6"),sQuery(id+"F2.wireOp",EDGE,"E2.5.1.7"),sQuery(id+"F2.wireOp",EDGE,"E2.5.1.8"),sQuery(id+"F2.wireOp",EDGE,"E2.5.1.9"),sQuery(id+"F2.wireOp",EDGE,"E2.5.1.10"),sQuery(id+"F2.wireOp",EDGE,"E2.5.1.11"),sQuery(id+"F2.wireOp",EDGE,"E2.5.1.13"),sQuery(id+"F2.wireOp",EDGE,"E2.5.2.1"),sQuery(id+"F2.wireOp",EDGE,"E2.5.2.2"),sQuery(id+"F2.wireOp",EDGE,"E2.5.2.3"),sQuery(id+"F2.wireOp",EDGE,"E2.5.2.4"),sQuery(id+"F2.wireOp",EDGE,"E2.5.2.5"),sQuery(id+"F2.wireOp",EDGE,"E2.5.2.6"),sQuery(id+"F2.wireOp",EDGE,"E2.5.2.7"),sQuery(id+"F2.wireOp",EDGE,"E2.5.2.8"),sQuery(id+"F2.wireOp",EDGE,"E2.5.2.9"),sQuery(id+"F2.wireOp",EDGE,"E2.5.2.10"),sQuery(id+"F2.wireOp",EDGE,"E2.5.2.11"),sQuery(id+"F2.wireOp",EDGE,"E2.5.2.13"),sQuery(id+"F2.wireOp",EDGE,"E2.5.3.1"),sQuery(id+"F2.wireOp",EDGE,"E2.5.3.2"),sQuery(id+"F2.wireOp",EDGE,"E2.5.3.3"),sQuery(id+"F2.wireOp",EDGE,"E2.5.3.4"),sQuery(id+"F2.wireOp",EDGE,"E2.5.3.5"),sQuery(id+"F2.wireOp",EDGE,"E2.5.3.10"),sQuery(id+"F2.wireOp",EDGE,"E2.5.3.11"),sQuery(id+"F2.wireOp",EDGE,"E2.5.3.13"),sQuery(id+"F2.wireOp",EDGE,"E2.6.0.7"),sQuery(id+"F2.wireOp",EDGE,"E2.6.0.8"),sQuery(id+"F2.wireOp",EDGE,"E2.6.1.2"),sQuery(id+"F2.wireOp",EDGE,"E2.6.1.3"),sQuery(id+"F2.wireOp",EDGE,"E2.6.1.4"),sQuery(id+"F2.wireOp",EDGE,"E2.6.1.7"),sQuery(id+"F2.wireOp",EDGE,"E2.6.1.8"),sQuery(id+"F2.wireOp",EDGE,"E2.6.1.9"),sQuery(id+"F2.wireOp",EDGE,"E2.6.1.10"),sQuery(id+"F2.wireOp",EDGE,"E2.6.1.11"),sQuery(id+"F2.wireOp",EDGE,"E2.6.2.2"),sQuery(id+"F2.wireOp",EDGE,"E2.6.2.3"),sQuery(id+"F2.wireOp",EDGE,"E2.6.2.4"),sQuery(id+"F2.wireOp",EDGE,"E2.6.2.7"),sQuery(id+"F2.wireOp",EDGE,"E2.6.2.8"),sQuery(id+"F2.wireOp",EDGE,"E2.6.2.9"),sQuery(id+"F2.wireOp",EDGE,"E2.6.2.10"),sQuery(id+"F2.wireOp",EDGE,"E2.6.2.11"),sQuery(id+"F2.wireOp",EDGE,"E2.6.3.2"),sQuery(id+"F2.wireOp",EDGE,"E2.6.3.3"),sQuery(id+"F2.wireOp",EDGE,"E2.6.3.4"),sQuery(id+"F2.wireOp",EDGE,"E2.6.3.10"),sQuery(id+"F2.wireOp",EDGE,"E2.6.3.11"),sQuery(id+"F2.wireOp",EDGE,"E3.0"),sQuery(id+"F2.wireOp",EDGE,"E3.1"),sQuery(id+"F2.wireOp",EDGE,"E3.2"),sQuery(id+"F2.wireOp",EDGE,"E3.3"),sQuery(id+"F2.wireOp",EDGE,"E4.trimOffspring"),sQuery(id+"F2.wireOp",EDGE,"E5.trimOffspring"),sQuery(id+"F2.wireOp",EDGE,"E6.trimOffspring"),sQuery(id+"F2.wireOp",EDGE,"E7.trimOffspring"),sQuery(id+"F2.wireOp",EDGE,"E8.trimOffspring"),sQuery(id+"F2.wireOp",EDGE,"E9.trimOffspring"),sQuery(id+"F2.wireOp",EDGE,"E10.trimOffspring"),sQuery(id+"F2.wireOp",EDGE,"E11.trimOffspring"),sQuery(id+"F2.wireOp",EDGE,"E12.trimOffspring"),sQuery(id+"F2.wireOp",EDGE,"E13.trimOffspring"),sQuery(id+"F2.wireOp",EDGE,"E14.trimOffspring"),sQuery(id+"F2.wireOp",EDGE,"E15.trimOffspring"),sQuery(id+"F2.wireOp",EDGE,"E16.trimOffspring"),sQuery(id+"F2.wireOp",EDGE,"E17.trimOffspring"),sQuery(id+"F2.wireOp",EDGE,"E18.trimOffspring"),sQuery(id+"F2.wireOp",EDGE,"E19.trimOffspring"),sQuery(id+"F2.wireOp",EDGE,"E20.trimOffspring"),sQuery(id+"F2.wireOp",EDGE,"E21.trimOffspring"),sQuery(id+"F2.wireOp",EDGE,"E22.trimOffspring"),sQuery(id+"F2.wireOp",EDGE,"E23.trimOffspring"),sQuery(id+"F2.wireOp",EDGE,"E24.trimOffspring"),sQuery(id+"F2.wireOp",EDGE,"E25.trimOffspring"),sQuery(id+"F2.wireOp",EDGE,"E26.0"),sQuery(id+"F2.wireOp",EDGE,"E26.1"),sQuery(id+"F2.wireOp",EDGE,"E26.2"),sQuery(id+"F2.wireOp",EDGE,"E26.3")])],"isStart":false})]});
            extrude(context, id + "F7", {"entities" : qUnion([Q0]), "operationType" : NewBodyOperationType.ADD, "endBound" : BoundingType.UP_TO_SURFACE, "endBoundEntityFace" : qUnion([Q1]), "depth" : 4 * mm});
        }
        {
            var Q0;
            Q0=qCreatedBy(makeId("Top.planeOp"),FACE);
            var sketch = newSketch(context, id + "F8", { "sketchPlane" : qUnion([Q0])});
            skCircle(sketch, "E34.cCircle", {"center": v(-72, 41.57) * mm, "radius": 11.55 * mm, "construction": true});
            skLineSegment(sketch, "E34.3", {"start": v(-72, 53.12) * mm, "end": v(-62, 47.34) * mm});
            skLineSegment(sketch, "E34.4", {"start": v(-62, 47.34) * mm, "end": v(-62, 35.8) * mm});
            skLineSegment(sketch, "E34.5", {"start": v(-62, 35.8) * mm, "end": v(-72, 30.02) * mm});
            skCircle(sketch, "E35.cCircle", {"center": v(-72, -41.57) * mm, "radius": 11.55 * mm, "construction": true});
            skLineSegment(sketch, "E35.0", {"start": v(-62, -47.34) * mm, "end": v(-72, -53.12) * mm});
            skLineSegment(sketch, "E35.4", {"start": v(-72, -30.02) * mm, "end": v(-62, -35.8) * mm});
            skLineSegment(sketch, "E35.5", {"start": v(-62, -35.8) * mm, "end": v(-62, -47.34) * mm});
            skLineSegment(sketch, "E36.0", {"start": v(-70, -59) * mm, "end": v(-70, -6.35) * mm});
            skLineSegment(sketch, "E37.0", {"start": v(-70, 6.35) * mm, "end": v(-70, 59) * mm});
            skSolve(sketch);
        }
        {
            var Q0;
            Q0 = qSketchRegion(id + "F8", true);
            var Q1;
            Q1=makeQuery(id+"F7.boolean.opBoolean","MERGE",FACE,{"derivedFrom":[makeQuery(id+"F3.boolean.opBoolean","MERGE",FACE,{"derivedFrom":[makeQuery(id+"F1.opExtrude","CAP_FACE",FACE,{"disambiguationData":[OSD([sQuery(id+"F0.wireOp",EDGE,"E0.bottom"),sQuery(id+"F0.wireOp",EDGE,"E0.top"),sQuery(id+"F0.wireOp",EDGE,"E0.left"),sQuery(id+"F0.wireOp",EDGE,"E0.right"),sQuery(id+"F0.wireOp",EDGE,"E1.0"),sQuery(id+"F0.wireOp",EDGE,"E1.1"),sQuery(id+"F0.wireOp",EDGE,"E1.2"),sQuery(id+"F0.wireOp",EDGE,"E1.3")])],"isStart":false}),makeQuery(id+"F3.opExtrude","CAP_FACE",FACE,{"disambiguationData":[OSD([sQuery(id+"F2.wireOp",EDGE,"E2.0.1.1"),sQuery(id+"F2.wireOp",EDGE,"E2.0.1.5"),sQuery(id+"F2.wireOp",EDGE,"E2.0.1.13"),sQuery(id+"F2.wireOp",EDGE,"E2.0.2.1"),sQuery(id+"F2.wireOp",EDGE,"E2.0.2.5"),sQuery(id+"F2.wireOp",EDGE,"E2.0.2.13"),sQuery(id+"F2.wireOp",EDGE,"E2.0.3.1"),sQuery(id+"F2.wireOp",EDGE,"E2.0.3.5"),sQuery(id+"F2.wireOp",EDGE,"E2.0.3.13"),sQuery(id+"F2.wireOp",EDGE,"E2.1.0.7"),sQuery(id+"F2.wireOp",EDGE,"E2.1.0.8"),sQuery(id+"F2.wireOp",EDGE,"E2.1.1.1"),sQuery(id+"F2.wireOp",EDGE,"E2.1.1.2"),sQuery(id+"F2.wireOp",EDGE,"E2.1.1.3"),sQuery(id+"F2.wireOp",EDGE,"E2.1.1.4"),sQuery(id+"F2.wireOp",EDGE,"E2.1.1.5"),sQuery(id+"F2.wireOp",EDGE,"E2.1.1.6"),sQuery(id+"F2.wireOp",EDGE,"E2.1.1.7"),sQuery(id+"F2.wireOp",EDGE,"E2.1.1.8"),sQuery(id+"F2.wireOp",EDGE,"E2.1.1.10"),sQuery(id+"F2.wireOp",EDGE,"E2.1.1.11"),sQuery(id+"F2.wireOp",EDGE,"E2.1.1.13"),sQuery(id+"F2.wireOp",EDGE,"E2.1.2.1"),sQuery(id+"F2.wireOp",EDGE,"E2.1.2.2"),sQuery(id+"F2.wireOp",EDGE,"E2.1.2.3"),sQuery(id+"F2.wireOp",EDGE,"E2.1.2.4"),sQuery(id+"F2.wireOp",EDGE,"E2.1.2.5"),sQuery(id+"F2.wireOp",EDGE,"E2.1.2.6"),sQuery(id+"F2.wireOp",EDGE,"E2.1.2.7"),sQuery(id+"F2.wireOp",EDGE,"E2.1.2.8"),sQuery(id+"F2.wireOp",EDGE,"E2.1.2.10"),sQuery(id+"F2.wireOp",EDGE,"E2.1.2.11"),sQuery(id+"F2.wireOp",EDGE,"E2.1.2.13"),sQuery(id+"F2.wireOp",EDGE,"E2.1.3.1"),sQuery(id+"F2.wireOp",EDGE,"E2.1.3.2"),sQuery(id+"F2.wireOp",EDGE,"E2.1.3.3"),sQuery(id+"F2.wireOp",EDGE,"E2.1.3.4"),sQuery(id+"F2.wireOp",EDGE,"E2.1.3.5"),sQuery(id+"F2.wireOp",EDGE,"E2.1.3.10"),sQuery(id+"F2.wireOp",EDGE,"E2.1.3.11"),sQuery(id+"F2.wireOp",EDGE,"E2.1.3.13"),sQuery(id+"F2.wireOp",EDGE,"E2.2.0.7"),sQuery(id+"F2.wireOp",EDGE,"E2.2.0.8"),sQuery(id+"F2.wireOp",EDGE,"E2.2.1.1"),sQuery(id+"F2.wireOp",EDGE,"E2.2.1.2"),sQuery(id+"F2.wireOp",EDGE,"E2.2.1.3"),sQuery(id+"F2.wireOp",EDGE,"E2.2.1.4"),sQuery(id+"F2.wireOp",EDGE,"E2.2.1.5"),sQuery(id+"F2.wireOp",EDGE,"E2.2.1.6"),sQuery(id+"F2.wireOp",EDGE,"E2.2.1.7"),sQuery(id+"F2.wireOp",EDGE,"E2.2.1.8"),sQuery(id+"F2.wireOp",EDGE,"E2.2.1.9"),sQuery(id+"F2.wireOp",EDGE,"E2.2.1.10"),sQuery(id+"F2.wireOp",EDGE,"E2.2.1.11"),sQuery(id+"F2.wireOp",EDGE,"E2.2.1.13"),sQuery(id+"F2.wireOp",EDGE,"E2.2.2.1"),sQuery(id+"F2.wireOp",EDGE,"E2.2.2.2"),sQuery(id+"F2.wireOp",EDGE,"E2.2.2.3"),sQuery(id+"F2.wireOp",EDGE,"E2.2.2.4"),sQuery(id+"F2.wireOp",EDGE,"E2.2.2.5"),sQuery(id+"F2.wireOp",EDGE,"E2.2.2.6"),sQuery(id+"F2.wireOp",EDGE,"E2.2.2.7"),sQuery(id+"F2.wireOp",EDGE,"E2.2.2.8"),sQuery(id+"F2.wireOp",EDGE,"E2.2.2.9"),sQuery(id+"F2.wireOp",EDGE,"E2.2.2.10"),sQuery(id+"F2.wireOp",EDGE,"E2.2.2.11"),sQuery(id+"F2.wireOp",EDGE,"E2.2.2.13"),sQuery(id+"F2.wireOp",EDGE,"E2.2.3.1"),sQuery(id+"F2.wireOp",EDGE,"E2.2.3.2"),sQuery(id+"F2.wireOp",EDGE,"E2.2.3.3"),sQuery(id+"F2.wireOp",EDGE,"E2.2.3.4"),sQuery(id+"F2.wireOp",EDGE,"E2.2.3.5"),sQuery(id+"F2.wireOp",EDGE,"E2.2.3.10"),sQuery(id+"F2.wireOp",EDGE,"E2.2.3.11"),sQuery(id+"F2.wireOp",EDGE,"E2.2.3.13"),sQuery(id+"F2.wireOp",EDGE,"E2.3.0.7"),sQuery(id+"F2.wireOp",EDGE,"E2.3.0.8"),sQuery(id+"F2.wireOp",EDGE,"E2.3.1.1"),sQuery(id+"F2.wireOp",EDGE,"E2.3.1.2"),sQuery(id+"F2.wireOp",EDGE,"E2.3.1.3"),sQuery(id+"F2.wireOp",EDGE,"E2.3.1.4"),sQuery(id+"F2.wireOp",EDGE,"E2.3.1.5"),sQuery(id+"F2.wireOp",EDGE,"E2.3.1.6"),sQuery(id+"F2.wireOp",EDGE,"E2.3.1.7"),sQuery(id+"F2.wireOp",EDGE,"E2.3.1.8"),sQuery(id+"F2.wireOp",EDGE,"E2.3.1.9"),sQuery(id+"F2.wireOp",EDGE,"E2.3.1.10"),sQuery(id+"F2.wireOp",EDGE,"E2.3.1.11"),sQuery(id+"F2.wireOp",EDGE,"E2.3.1.13"),sQuery(id+"F2.wireOp",EDGE,"E2.3.2.1"),sQuery(id+"F2.wireOp",EDGE,"E2.3.2.2"),sQuery(id+"F2.wireOp",EDGE,"E2.3.2.3"),sQuery(id+"F2.wireOp",EDGE,"E2.3.2.4"),sQuery(id+"F2.wireOp",EDGE,"E2.3.2.5"),sQuery(id+"F2.wireOp",EDGE,"E2.3.2.6"),sQuery(id+"F2.wireOp",EDGE,"E2.3.2.7"),sQuery(id+"F2.wireOp",EDGE,"E2.3.2.8"),sQuery(id+"F2.wireOp",EDGE,"E2.3.2.9"),sQuery(id+"F2.wireOp",EDGE,"E2.3.2.10"),sQuery(id+"F2.wireOp",EDGE,"E2.3.2.11"),sQuery(id+"F2.wireOp",EDGE,"E2.3.2.13"),sQuery(id+"F2.wireOp",EDGE,"E2.3.3.1"),sQuery(id+"F2.wireOp",EDGE,"E2.3.3.2"),sQuery(id+"F2.wireOp",EDGE,"E2.3.3.3"),sQuery(id+"F2.wireOp",EDGE,"E2.3.3.4"),sQuery(id+"F2.wireOp",EDGE,"E2.3.3.5"),sQuery(id+"F2.wireOp",EDGE,"E2.3.3.10"),sQuery(id+"F2.wireOp",EDGE,"E2.3.3.11"),sQuery(id+"F2.wireOp",EDGE,"E2.3.3.13"),sQuery(id+"F2.wireOp",EDGE,"E2.4.0.7"),sQuery(id+"F2.wireOp",EDGE,"E2.4.0.8"),sQuery(id+"F2.wireOp",EDGE,"E2.4.1.1"),sQuery(id+"F2.wireOp",EDGE,"E2.4.1.2"),sQuery(id+"F2.wireOp",EDGE,"E2.4.1.3"),sQuery(id+"F2.wireOp",EDGE,"E2.4.1.4"),sQuery(id+"F2.wireOp",EDGE,"E2.4.1.5"),sQuery(id+"F2.wireOp",EDGE,"E2.4.1.6"),sQuery(id+"F2.wireOp",EDGE,"E2.4.1.7"),sQuery(id+"F2.wireOp",EDGE,"E2.4.1.8"),sQuery(id+"F2.wireOp",EDGE,"E2.4.1.9"),sQuery(id+"F2.wireOp",EDGE,"E2.4.1.10"),sQuery(id+"F2.wireOp",EDGE,"E2.4.1.11"),sQuery(id+"F2.wireOp",EDGE,"E2.4.1.13"),sQuery(id+"F2.wireOp",EDGE,"E2.4.2.1"),sQuery(id+"F2.wireOp",EDGE,"E2.4.2.2"),sQuery(id+"F2.wireOp",EDGE,"E2.4.2.3"),sQuery(id+"F2.wireOp",EDGE,"E2.4.2.4"),sQuery(id+"F2.wireOp",EDGE,"E2.4.2.5"),sQuery(id+"F2.wireOp",EDGE,"E2.4.2.6"),sQuery(id+"F2.wireOp",EDGE,"E2.4.2.7"),sQuery(id+"F2.wireOp",EDGE,"E2.4.2.8"),sQuery(id+"F2.wireOp",EDGE,"E2.4.2.9"),sQuery(id+"F2.wireOp",EDGE,"E2.4.2.10"),sQuery(id+"F2.wireOp",EDGE,"E2.4.2.11"),sQuery(id+"F2.wireOp",EDGE,"E2.4.2.13"),sQuery(id+"F2.wireOp",EDGE,"E2.4.3.1"),sQuery(id+"F2.wireOp",EDGE,"E2.4.3.2"),sQuery(id+"F2.wireOp",EDGE,"E2.4.3.3"),sQuery(id+"F2.wireOp",EDGE,"E2.4.3.4"),sQuery(id+"F2.wireOp",EDGE,"E2.4.3.5"),sQuery(id+"F2.wireOp",EDGE,"E2.4.3.10"),sQuery(id+"F2.wireOp",EDGE,"E2.4.3.11"),sQuery(id+"F2.wireOp",EDGE,"E2.4.3.13"),sQuery(id+"F2.wireOp",EDGE,"E2.5.0.7"),sQuery(id+"F2.wireOp",EDGE,"E2.5.0.8"),sQuery(id+"F2.wireOp",EDGE,"E2.5.1.1"),sQuery(id+"F2.wireOp",EDGE,"E2.5.1.2"),sQuery(id+"F2.wireOp",EDGE,"E2.5.1.3"),sQuery(id+"F2.wireOp",EDGE,"E2.5.1.4"),sQuery(id+"F2.wireOp",EDGE,"E2.5.1.5"),sQuery(id+"F2.wireOp",EDGE,"E2.5.1.6"),sQuery(id+"F2.wireOp",EDGE,"E2.5.1.7"),sQuery(id+"F2.wireOp",EDGE,"E2.5.1.8"),sQuery(id+"F2.wireOp",EDGE,"E2.5.1.9"),sQuery(id+"F2.wireOp",EDGE,"E2.5.1.10"),sQuery(id+"F2.wireOp",EDGE,"E2.5.1.11"),sQuery(id+"F2.wireOp",EDGE,"E2.5.1.13"),sQuery(id+"F2.wireOp",EDGE,"E2.5.2.1"),sQuery(id+"F2.wireOp",EDGE,"E2.5.2.2"),sQuery(id+"F2.wireOp",EDGE,"E2.5.2.3"),sQuery(id+"F2.wireOp",EDGE,"E2.5.2.4"),sQuery(id+"F2.wireOp",EDGE,"E2.5.2.5"),sQuery(id+"F2.wireOp",EDGE,"E2.5.2.6"),sQuery(id+"F2.wireOp",EDGE,"E2.5.2.7"),sQuery(id+"F2.wireOp",EDGE,"E2.5.2.8"),sQuery(id+"F2.wireOp",EDGE,"E2.5.2.9"),sQuery(id+"F2.wireOp",EDGE,"E2.5.2.10"),sQuery(id+"F2.wireOp",EDGE,"E2.5.2.11"),sQuery(id+"F2.wireOp",EDGE,"E2.5.2.13"),sQuery(id+"F2.wireOp",EDGE,"E2.5.3.1"),sQuery(id+"F2.wireOp",EDGE,"E2.5.3.2"),sQuery(id+"F2.wireOp",EDGE,"E2.5.3.3"),sQuery(id+"F2.wireOp",EDGE,"E2.5.3.4"),sQuery(id+"F2.wireOp",EDGE,"E2.5.3.5"),sQuery(id+"F2.wireOp",EDGE,"E2.5.3.10"),sQuery(id+"F2.wireOp",EDGE,"E2.5.3.11"),sQuery(id+"F2.wireOp",EDGE,"E2.5.3.13"),sQuery(id+"F2.wireOp",EDGE,"E2.6.0.7"),sQuery(id+"F2.wireOp",EDGE,"E2.6.0.8"),sQuery(id+"F2.wireOp",EDGE,"E2.6.1.2"),sQuery(id+"F2.wireOp",EDGE,"E2.6.1.3"),sQuery(id+"F2.wireOp",EDGE,"E2.6.1.4"),sQuery(id+"F2.wireOp",EDGE,"E2.6.1.7"),sQuery(id+"F2.wireOp",EDGE,"E2.6.1.8"),sQuery(id+"F2.wireOp",EDGE,"E2.6.1.9"),sQuery(id+"F2.wireOp",EDGE,"E2.6.1.10"),sQuery(id+"F2.wireOp",EDGE,"E2.6.1.11"),sQuery(id+"F2.wireOp",EDGE,"E2.6.2.2"),sQuery(id+"F2.wireOp",EDGE,"E2.6.2.3"),sQuery(id+"F2.wireOp",EDGE,"E2.6.2.4"),sQuery(id+"F2.wireOp",EDGE,"E2.6.2.7"),sQuery(id+"F2.wireOp",EDGE,"E2.6.2.8"),sQuery(id+"F2.wireOp",EDGE,"E2.6.2.9"),sQuery(id+"F2.wireOp",EDGE,"E2.6.2.10"),sQuery(id+"F2.wireOp",EDGE,"E2.6.2.11"),sQuery(id+"F2.wireOp",EDGE,"E2.6.3.2"),sQuery(id+"F2.wireOp",EDGE,"E2.6.3.3"),sQuery(id+"F2.wireOp",EDGE,"E2.6.3.4"),sQuery(id+"F2.wireOp",EDGE,"E2.6.3.10"),sQuery(id+"F2.wireOp",EDGE,"E2.6.3.11"),sQuery(id+"F2.wireOp",EDGE,"E3.0"),sQuery(id+"F2.wireOp",EDGE,"E3.1"),sQuery(id+"F2.wireOp",EDGE,"E3.2"),sQuery(id+"F2.wireOp",EDGE,"E3.3"),sQuery(id+"F2.wireOp",EDGE,"E4.trimOffspring"),sQuery(id+"F2.wireOp",EDGE,"E5.trimOffspring"),sQuery(id+"F2.wireOp",EDGE,"E6.trimOffspring"),sQuery(id+"F2.wireOp",EDGE,"E7.trimOffspring"),sQuery(id+"F2.wireOp",EDGE,"E8.trimOffspring"),sQuery(id+"F2.wireOp",EDGE,"E9.trimOffspring"),sQuery(id+"F2.wireOp",EDGE,"E10.trimOffspring"),sQuery(id+"F2.wireOp",EDGE,"E11.trimOffspring"),sQuery(id+"F2.wireOp",EDGE,"E12.trimOffspring"),sQuery(id+"F2.wireOp",EDGE,"E13.trimOffspring"),sQuery(id+"F2.wireOp",EDGE,"E14.trimOffspring"),sQuery(id+"F2.wireOp",EDGE,"E15.trimOffspring"),sQuery(id+"F2.wireOp",EDGE,"E16.trimOffspring"),sQuery(id+"F2.wireOp",EDGE,"E17.trimOffspring"),sQuery(id+"F2.wireOp",EDGE,"E18.trimOffspring"),sQuery(id+"F2.wireOp",EDGE,"E19.trimOffspring"),sQuery(id+"F2.wireOp",EDGE,"E20.trimOffspring"),sQuery(id+"F2.wireOp",EDGE,"E21.trimOffspring"),sQuery(id+"F2.wireOp",EDGE,"E22.trimOffspring"),sQuery(id+"F2.wireOp",EDGE,"E23.trimOffspring"),sQuery(id+"F2.wireOp",EDGE,"E24.trimOffspring"),sQuery(id+"F2.wireOp",EDGE,"E25.trimOffspring"),sQuery(id+"F2.wireOp",EDGE,"E26.0"),sQuery(id+"F2.wireOp",EDGE,"E26.1"),sQuery(id+"F2.wireOp",EDGE,"E26.2"),sQuery(id+"F2.wireOp",EDGE,"E26.3")])],"isStart":false})]}),makeQuery(id+"F7.opExtrude","CAP_FACE",FACE,{"disambiguationData":[OSD([sQuery(id+"F6.wireOp",EDGE,"E32.0"),sQuery(id+"F6.wireOp",EDGE,"E32.1"),sQuery(id+"F6.wireOp",EDGE,"E32.2"),sQuery(id+"F6.wireOp",EDGE,"E33.0")])],"isStart":false})]});
            extrude(context, id + "F9", {"entities" : qUnion([Q0]), "operationType" : NewBodyOperationType.ADD, "endBound" : BoundingType.UP_TO_SURFACE, "endBoundEntityFace" : qUnion([Q1]), "depth" : 25 * mm});
        }
        {
            var Q0;
            Q0=qCreatedBy(makeId("Top.planeOp"),FACE);
            var sketch = newSketch(context, id + "F10", { "sketchPlane" : qUnion([Q0])});
            skLineSegment(sketch, "E38.0", {"start": v(-66, 49.65) * mm, "end": v(-62, 47.34) * mm, "construction": true});
            skLineSegment(sketch, "E38.1", {"start": v(-62, 47.34) * mm, "end": v(-62, 35.8) * mm, "construction": true});
            skLineSegment(sketch, "E38.2", {"start": v(-62, 35.8) * mm, "end": v(-66, 33.49) * mm, "construction": true});
            skLineSegment(sketch, "E38.3", {"start": v(-66, -33.49) * mm, "end": v(-62, -35.8) * mm, "construction": true});
            skLineSegment(sketch, "E38.4", {"start": v(-62, -35.8) * mm, "end": v(-62, -47.34) * mm, "construction": true});
            skLineSegment(sketch, "E38.5", {"start": v(-62, -47.34) * mm, "end": v(-66, -49.65) * mm, "construction": true});
            skCircle(sketch, "E39.cCircle", {"center": v(-72, 41.57) * mm, "radius": 11.55 * mm, "construction": true});
            skLineSegment(sketch, "E39.0", {"start": v(-62, 35.8) * mm, "end": v(-72, 30.02) * mm, "construction": true});
            skLineSegment(sketch, "E39.1", {"start": v(-72, 30.02) * mm, "end": v(-82, 35.8) * mm, "construction": true});
            skLineSegment(sketch, "E39.2", {"start": v(-82, 35.8) * mm, "end": v(-82, 47.34) * mm, "construction": true});
            skLineSegment(sketch, "E39.3", {"start": v(-82, 47.34) * mm, "end": v(-72, 53.12) * mm, "construction": true});
            skLineSegment(sketch, "E39.4", {"start": v(-72, 53.12) * mm, "end": v(-62, 47.34) * mm, "construction": true});
            skCircle(sketch, "E40.cCircle", {"center": v(-72, -41.57) * mm, "radius": 11.55 * mm, "construction": true});
            skLineSegment(sketch, "E40.0", {"start": v(-62, -47.34) * mm, "end": v(-72, -53.12) * mm, "construction": true});
            skLineSegment(sketch, "E40.1", {"start": v(-72, -53.12) * mm, "end": v(-82, -47.34) * mm, "construction": true});
            skLineSegment(sketch, "E40.2", {"start": v(-82, -47.34) * mm, "end": v(-82, -35.8) * mm, "construction": true});
            skLineSegment(sketch, "E40.3", {"start": v(-82, -35.8) * mm, "end": v(-72, -30.02) * mm, "construction": true});
            skLineSegment(sketch, "E40.4", {"start": v(-72, -30.02) * mm, "end": v(-62, -35.8) * mm, "construction": true});
            skLineSegment(sketch, "E41.0", {"start": v(-65, 37.53) * mm, "end": v(-73.5, 32.62) * mm});
            skLineSegment(sketch, "E41.1", {"start": v(-65, 45.61) * mm, "end": v(-65, 37.53) * mm});
            skLineSegment(sketch, "E41.2", {"start": v(-73.5, 50.52) * mm, "end": v(-65, 45.61) * mm});
            skLineSegment(sketch, "E42.0", {"start": v(-65, -45.61) * mm, "end": v(-73.5, -50.52) * mm});
            skLineSegment(sketch, "E42.1", {"start": v(-65, -37.53) * mm, "end": v(-65, -45.61) * mm});
            skLineSegment(sketch, "E42.2", {"start": v(-73.5, -32.62) * mm, "end": v(-65, -37.53) * mm});
            skLineSegment(sketch, "E43.0", {"start": v(-70, -59) * mm, "end": v(-70, -6.35) * mm});
            skLineSegment(sketch, "E44.0", {"start": v(-70, 6.35) * mm, "end": v(-70, 59) * mm});
            skSolve(sketch);
        }
        {
            var Q0;
            Q0 = qSketchRegion(id + "F10", true);
            extrude(context, id + "F11", {"entities" : qUnion([Q0]), "operationType" : NewBodyOperationType.REMOVE, "endBound" : BoundingType.THROUGH_ALL, "depth" : 25 * mm});
        }
    });
